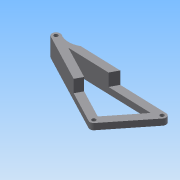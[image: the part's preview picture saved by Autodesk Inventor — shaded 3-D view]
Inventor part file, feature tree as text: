
AUTODESK INVENTOR PART (.ipt)
format: ipt  version: 2015 (Build 190159000, 159)  size: 135,168 bytes
history: native  units: mm
features: sketch x6, extrude x4, other x3
ambient origin geometry x8: Origin, YZ Plane, XZ Plane, XY Plane, X Axis, Y Axis, Z Axis, Center Point
bodies: Body1 (feature_tree)
feature tree (13):
  other  "實體1"
  extrude  "擠出1"  Depth=28.86mm
  extrude  "擠出2"  Depth=35.28mm
  extrude  "擠出3"  Depth=15.61mm
  extrude  "擠出4"  Depth=2.5mm
  other  "迴轉2"
  other  "迴轉1"
  sketch  "草圖1"
  sketch  "草圖2"
  sketch  "草圖3"
  sketch  "草圖4"
  sketch  "草圖5"
  sketch  "草圖6"
